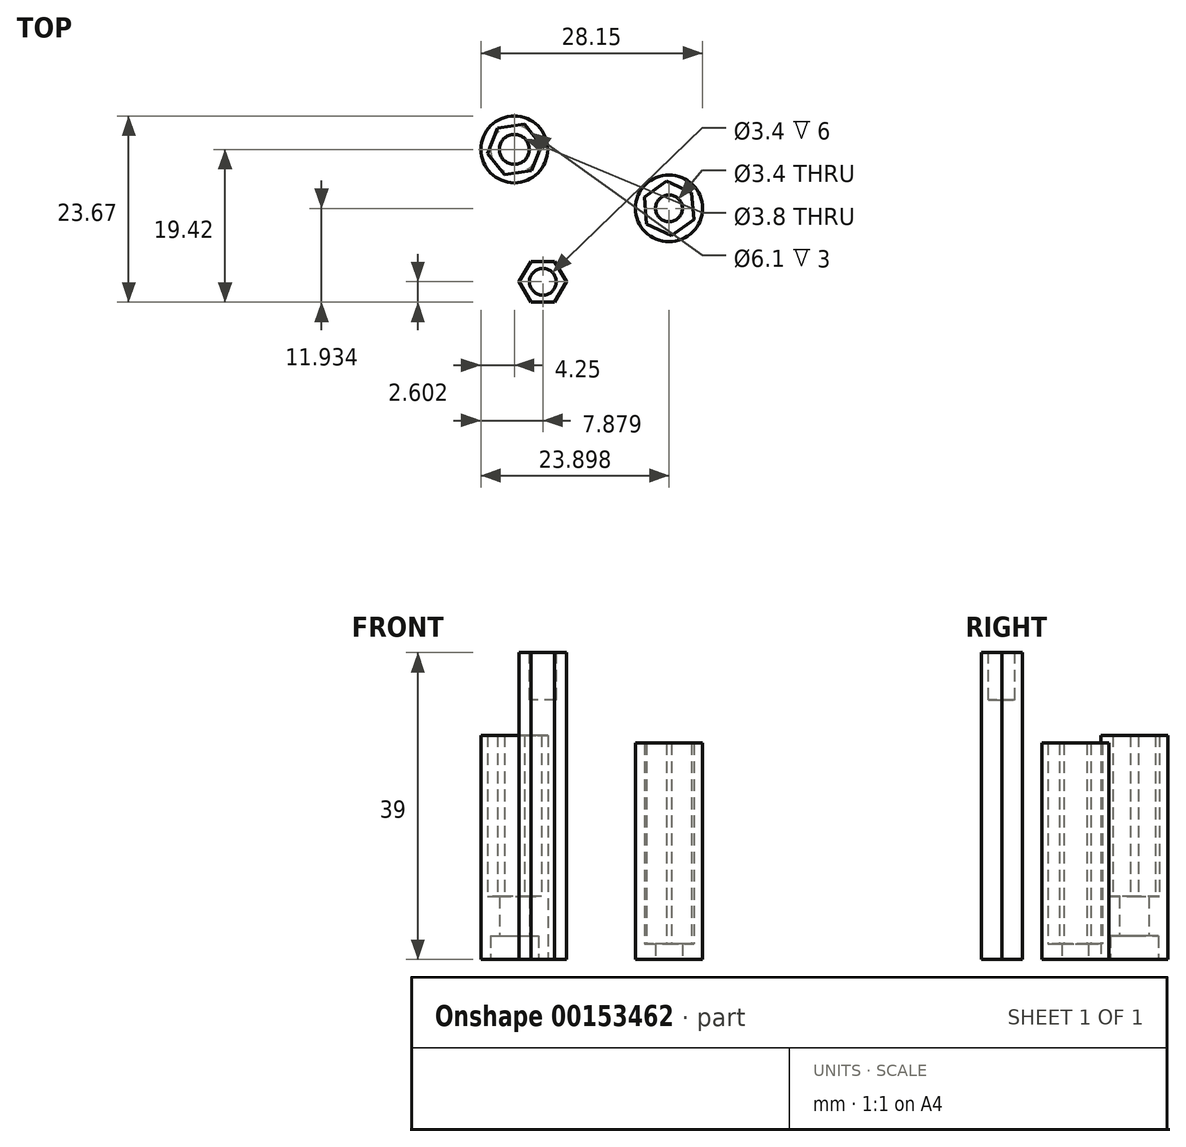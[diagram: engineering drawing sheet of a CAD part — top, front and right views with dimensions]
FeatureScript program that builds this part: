
annotation { "Feature Type Name" : "Feature", "Feature Type Description" : "" }
export const myFeature = defineFeature(function(context is Context, id is Id, definition is map)
    precondition{}
    {
        {
            var Q0;
            Q0=qCreatedBy(makeId("Top.planeOp"),FACE);
            var sketch = newSketch(context, id + "F0", { "sketchPlane" : qUnion([Q0])});
            skCircle(sketch, "E0", {"center": v(0, 0) * mm, "radius": 4.25 * mm});
            skCircle(sketch, "E1", {"center": v(0, 0) * mm, "radius": 1.9 * mm});
            skSolve(sketch);
        }
        {
            var Q0;
            Q0=makeQuery(id+"F0.imprint","IMPRINT",FACE,{"disambiguationData":[TD([[makeQuery(id+"F0.imprint","IMPRINT",EDGE,{"derivedFrom":sQuery(id+"F0.wireOp",EDGE,"E0")}),1.0]])]});
            extrude(context, id + "F1", {"entities" : qUnion([Q0]), "depth" : 8 * mm});
        }
        {
            var Q0;
            Q0=makeQuery(id+"F1.opExtrude","CAP_FACE",FACE,{"disambiguationData":[OSD([sQuery(id+"F0.wireOp",EDGE,"E0"),sQuery(id+"F0.wireOp",EDGE,"E1")])],"isStart":true});
            var sketch = newSketch(context, id + "F2", { "sketchPlane" : qUnion([Q0])});
            skCircle(sketch, "E2", {"center": v(0, 0) * mm, "radius": 3.05 * mm});
            skSolve(sketch);
        }
        {
            var Q0;
            Q0 = qSketchRegion(id + "F2", true);
            extrude(context, id + "F3", {"entities" : qUnion([Q0]), "operationType" : NewBodyOperationType.REMOVE, "oppositeDirection" : true, "depth" : 3 * mm});
        }
        {
            var Q0;
            Q0=makeQuery(id+"F1.opExtrude","CAP_FACE",FACE,{"disambiguationData":[OSD([sQuery(id+"F0.wireOp",EDGE,"E0"),sQuery(id+"F0.wireOp",EDGE,"E1")])],"isStart":false});
            var sketch = newSketch(context, id + "F4", { "sketchPlane" : qUnion([Q0])});
            skCircle(sketch, "E3.cCircle", {"center": v(0, 0) * mm, "radius": 3 * mm, "construction": true});
            skLineSegment(sketch, "E3.0", {"start": v(1.27, 3.22) * mm, "end": v(3.43, 0.51) * mm});
            skLineSegment(sketch, "E3.1", {"start": v(3.43, 0.51) * mm, "end": v(2.16, -2.71) * mm});
            skLineSegment(sketch, "E3.2", {"start": v(2.16, -2.71) * mm, "end": v(-1.27, -3.22) * mm});
            skLineSegment(sketch, "E3.3", {"start": v(-1.27, -3.22) * mm, "end": v(-3.43, -0.51) * mm});
            skLineSegment(sketch, "E3.4", {"start": v(-3.43, -0.51) * mm, "end": v(-2.16, 2.71) * mm});
            skLineSegment(sketch, "E3.5", {"start": v(-2.16, 2.71) * mm, "end": v(1.27, 3.22) * mm});
            skPoint(sketch, "E3.0.midPoint", {"position": v(2.35, 1.87) * mm});
            skSolve(sketch);
        }
        {
            var Q0;
            Q0=makeQuery(id+"F4.imprint","IMPRINT",FACE,{"disambiguationData":[TD([[makeQuery(id+"F4.imprint","IMPRINT",EDGE,{"derivedFrom":sQuery(id+"F4.wireOp",EDGE,"E3.0")}),1.0]])]});
            extrude(context, id + "F5", {"entities" : qUnion([Q0]), "operationType" : NewBodyOperationType.ADD, "depth" : 20.5 * mm});
        }
        {
            var Q0;
            Q0=qCreatedBy(makeId("Top.planeOp"),FACE);
            var sketch = newSketch(context, id + "F6", { "sketchPlane" : qUnion([Q0])});
            skCircle(sketch, "E4", {"center": v(19.65, -7.49) * mm, "radius": 4.25 * mm});
            skCircle(sketch, "E5", {"center": v(19.65, -7.49) * mm, "radius": 1.7 * mm});
            skSolve(sketch);
        }
        {
            var Q0;
            Q0 = qSketchRegion(id + "F6", true);
            extrude(context, id + "F7", {"entities" : qUnion([Q0]), "depth" : 2 * mm});
        }
        {
            var Q0;
            Q0=makeQuery(id+"F7.opExtrude","CAP_FACE",FACE,{"disambiguationData":[OSD([sQuery(id+"F6.wireOp",EDGE,"E4"),sQuery(id+"F6.wireOp",EDGE,"E5")])],"isStart":false});
            var sketch = newSketch(context, id + "F8", { "sketchPlane" : qUnion([Q0])});
            skCircle(sketch, "E6.cCircle", {"center": v(19.65, -7.49) * mm, "radius": 3 * mm, "construction": true});
            skLineSegment(sketch, "E6.0", {"start": v(19.33, -4.04) * mm, "end": v(22.48, -5.49) * mm});
            skLineSegment(sketch, "E6.1", {"start": v(22.48, -5.49) * mm, "end": v(22.8, -8.94) * mm});
            skLineSegment(sketch, "E6.2", {"start": v(22.8, -8.94) * mm, "end": v(19.96, -10.94) * mm});
            skLineSegment(sketch, "E6.3", {"start": v(19.96, -10.94) * mm, "end": v(16.82, -9.48) * mm});
            skLineSegment(sketch, "E6.4", {"start": v(16.82, -9.48) * mm, "end": v(16.5, -6.03) * mm});
            skLineSegment(sketch, "E6.5", {"start": v(16.5, -6.03) * mm, "end": v(19.33, -4.04) * mm});
            skPoint(sketch, "E6.0.midPoint", {"position": v(20.9, -4.76) * mm});
            skSolve(sketch);
        }
        {
            var Q0;
            Q0=makeQuery(id+"F8.imprint","IMPRINT",FACE,{"disambiguationData":[TD([[makeQuery(id+"F8.imprint","IMPRINT",EDGE,{"derivedFrom":sQuery(id+"F8.wireOp",EDGE,"E6.0")}),1.0]])]});
            extrude(context, id + "F9", {"entities" : qUnion([Q0]), "operationType" : NewBodyOperationType.ADD, "depth" : 25.5 * mm});
        }
        {
            var Q0;
            Q0=qCreatedBy(makeId("Top.planeOp"),FACE);
            var sketch = newSketch(context, id + "F10", { "sketchPlane" : qUnion([Q0])});
            skCircle(sketch, "E7.cCircle", {"center": v(3.63, -16.82) * mm, "radius": 2.6 * mm, "construction": true});
            skLineSegment(sketch, "E7.0", {"start": v(2.13, -14.22) * mm, "end": v(5.13, -14.22) * mm});
            skLineSegment(sketch, "E7.1", {"start": v(5.13, -14.22) * mm, "end": v(6.63, -16.82) * mm});
            skLineSegment(sketch, "E7.2", {"start": v(6.63, -16.82) * mm, "end": v(5.13, -19.42) * mm});
            skLineSegment(sketch, "E7.3", {"start": v(5.13, -19.42) * mm, "end": v(2.13, -19.42) * mm});
            skLineSegment(sketch, "E7.4", {"start": v(2.13, -19.42) * mm, "end": v(0.63, -16.82) * mm});
            skLineSegment(sketch, "E7.5", {"start": v(0.63, -16.82) * mm, "end": v(2.13, -14.22) * mm});
            skPoint(sketch, "E7.0.midPoint", {"position": v(3.63, -14.22) * mm});
            skSolve(sketch);
        }
        {
            var Q0;
            Q0 = qSketchRegion(id + "F10", true);
            extrude(context, id + "F11", {"entities" : qUnion([Q0]), "depth" : 39 * mm});
        }
        {
            var Q0;
            Q0=makeQuery(id+"F11.opExtrude","CAP_FACE",FACE,{"disambiguationData":[OSD([sQuery(id+"F10.wireOp",EDGE,"E7.0"),sQuery(id+"F10.wireOp",EDGE,"E7.1"),sQuery(id+"F10.wireOp",EDGE,"E7.2"),sQuery(id+"F10.wireOp",EDGE,"E7.3"),sQuery(id+"F10.wireOp",EDGE,"E7.4"),sQuery(id+"F10.wireOp",EDGE,"E7.5")])],"isStart":false});
            var sketch = newSketch(context, id + "F12", { "sketchPlane" : qUnion([Q0])});
            skCircle(sketch, "E8", {"center": v(3.63, -16.82) * mm, "radius": 1.7 * mm});
            skSolve(sketch);
        }
        {
            var Q0;
            Q0 = qSketchRegion(id + "F12", true);
            extrude(context, id + "F13", {"entities" : qUnion([Q0]), "operationType" : NewBodyOperationType.REMOVE, "oppositeDirection" : true, "depth" : 6 * mm});
        }
    });
